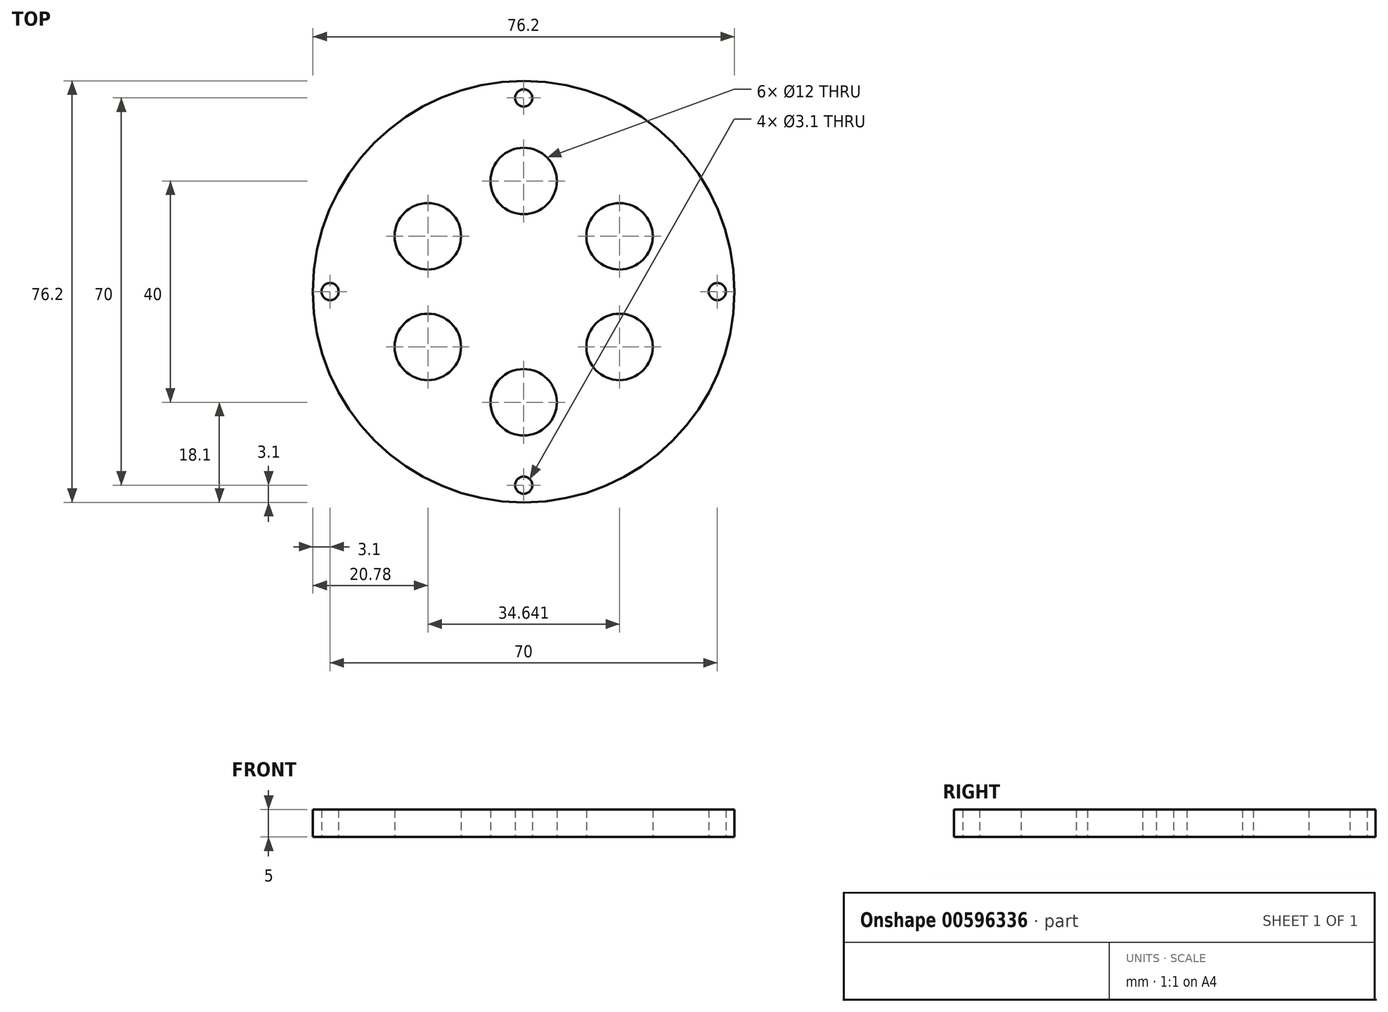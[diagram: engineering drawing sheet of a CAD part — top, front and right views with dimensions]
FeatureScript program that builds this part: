
annotation { "Feature Type Name" : "Feature", "Feature Type Description" : "" }
export const myFeature = defineFeature(function(context is Context, id is Id, definition is map)
    precondition{}
    {
        {
            var Q0;
            Q0=qCreatedBy(makeId("Top.planeOp"),FACE);
            var sketch = newSketch(context, id + "F0", { "sketchPlane" : qUnion([Q0])});
            skCircle(sketch, "E0", {"center": v(0, 0) * mm, "radius": 38.1 * mm});
            skCircle(sketch, "E1", {"center": v(0, 20) * mm, "radius": 6 * mm});
            skCircle(sketch, "E2", {"center": v(0, 35) * mm, "radius": 1.55 * mm});
            skCircle(sketch, "E3", {"center": v(0, 0) * mm, "radius": 7.5 * mm});
            skSolve(sketch);
        }
        {
            var Q0;
            Q0=makeQuery(id+"F0.imprint","IMPRINT",FACE,{"disambiguationData":[TD([[makeQuery(id+"F0.imprint","IMPRINT",EDGE,{"derivedFrom":sQuery(id+"F0.wireOp",EDGE,"E0")}),1.0]])]});
            var Q1;
            Q1=makeQuery(id+"F0.imprint","IMPRINT",FACE,{"disambiguationData":[TD([[makeQuery(id+"F0.imprint","IMPRINT",EDGE,{"derivedFrom":sQuery(id+"F0.wireOp",EDGE,"E1")}),1.0]])]});
            var Q2;
            Q2=makeQuery(id+"F0.imprint","IMPRINT",FACE,{"disambiguationData":[TD([[makeQuery(id+"F0.imprint","IMPRINT",EDGE,{"derivedFrom":sQuery(id+"F0.wireOp",EDGE,"E2")}),1.0]])]});
            extrude(context, id + "F1", {"entities" : qUnion([Q0, Q1, Q2]), "depth" : 5 * mm, "offsetDistance" : 25 * mm});
        }
        {
            var Q0;
            Q0=makeQuery(id+"F0.imprint","IMPRINT",FACE,{"disambiguationData":[TD([[makeQuery(id+"F0.imprint","IMPRINT",EDGE,{"derivedFrom":sQuery(id+"F0.wireOp",EDGE,"E1")}),1.0]])]});
            extrude(context, id + "F2", {"entities" : qUnion([Q0]), "depth" : 25 * mm, "offsetDistance" : 25 * mm});
        }
        {
            var Q0;
            Q0=makeQuery(id+"F2.opExtrude","SWEPT_BODY",BODY,{"disambiguationData":[OSD([sQuery(id+"F0.wireOp",EDGE,"E1")])]});
            var Q1;
            Q1=makeQuery(id+"F1.opExtrude","CAP_EDGE",EDGE,{"disambiguationData":[OSD([sQuery(id+"F0.wireOp",EDGE,"E0")])],"isStart":false});
            circularPattern(context, id + "F3", {"operationType" : NewBodyOperationType.REMOVE, "entities" : qUnion([Q0]), "axis" : qUnion([Q1]), "angle" : 360 * degree, "instanceCount" : 6, "equalSpace" : true});
        }
        {
            var Q0;
            Q0=makeQuery(id+"F0.imprint","IMPRINT",FACE,{"disambiguationData":[TD([[makeQuery(id+"F0.imprint","IMPRINT",EDGE,{"derivedFrom":sQuery(id+"F0.wireOp",EDGE,"E2")}),1.0]])]});
            extrude(context, id + "F4", {"entities" : qUnion([Q0]), "depth" : 25 * mm, "offsetDistance" : 25 * mm});
        }
        {
            var Q0;
            Q0=makeQuery(id+"F4.opExtrude","SWEPT_BODY",BODY,{"disambiguationData":[OSD([sQuery(id+"F0.wireOp",EDGE,"E2")])]});
            var Q1;
            Q1=makeQuery(id+"F1.opExtrude","CAP_EDGE",EDGE,{"disambiguationData":[OSD([sQuery(id+"F0.wireOp",EDGE,"E0")])],"isStart":false});
            circularPattern(context, id + "F5", {"operationType" : NewBodyOperationType.REMOVE, "entities" : qUnion([Q0]), "axis" : qUnion([Q1]), "angle" : 360 * degree, "instanceCount" : 4, "equalSpace" : true});
        }
        {
            var Q0;
            Q0=makeQuery(id+"F0.imprint","IMPRINT",FACE,{"disambiguationData":[TD([[makeQuery(id+"F0.imprint","IMPRINT",EDGE,{"derivedFrom":sQuery(id+"F0.wireOp",EDGE,"E3")}),1.0]])]});
            extrude(context, id + "F6", {"entities" : qUnion([Q0]), "operationType" : NewBodyOperationType.ADD, "depth" : 5 * mm, "offsetDistance" : 25 * mm});
        }
    });
